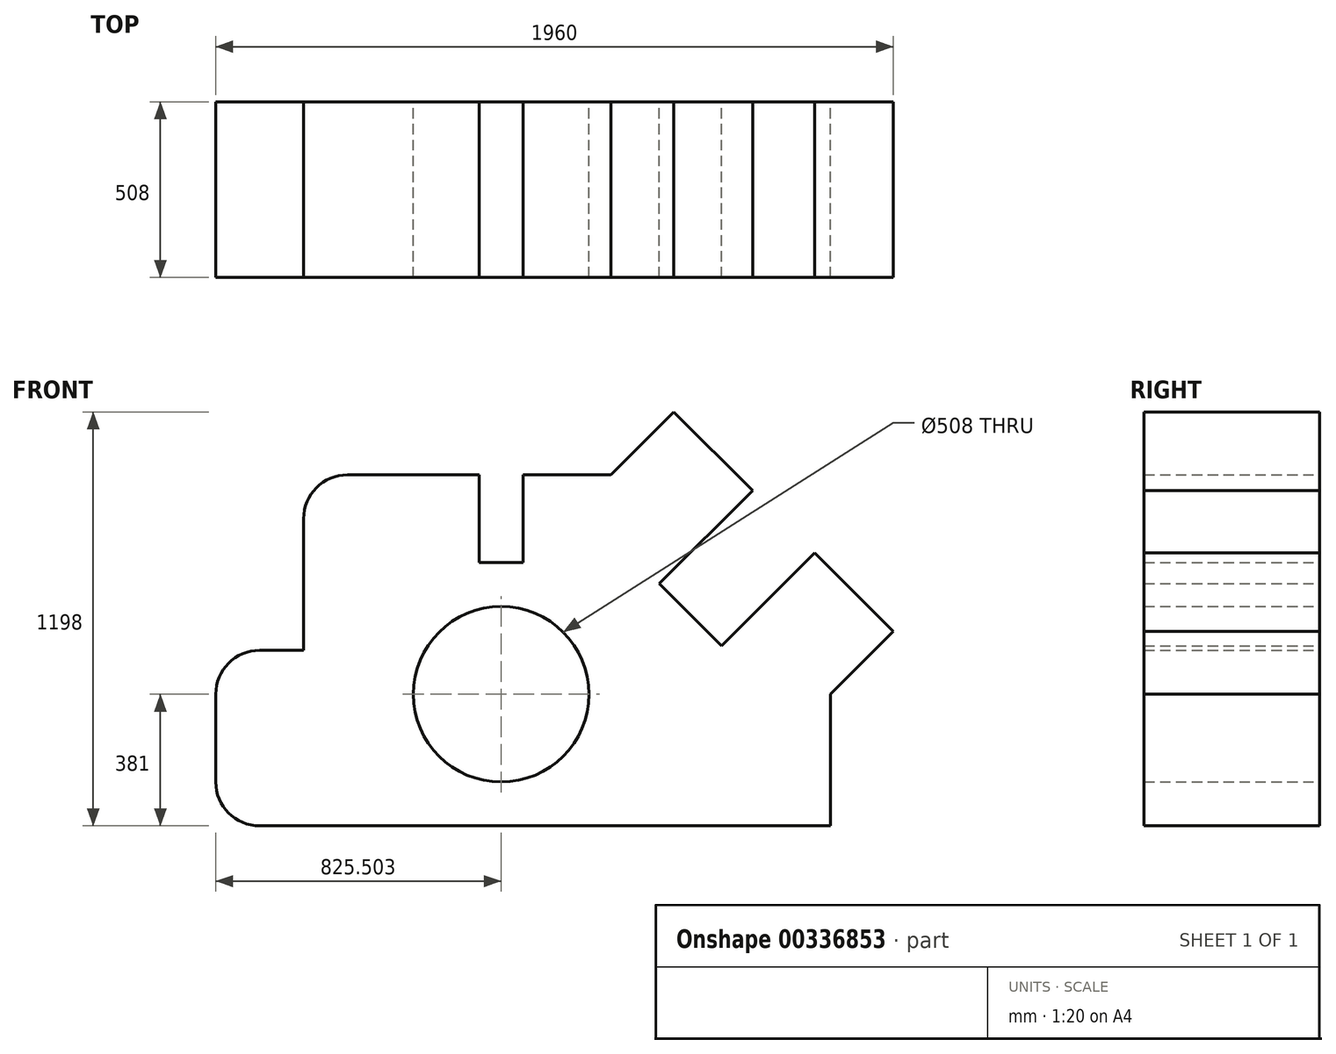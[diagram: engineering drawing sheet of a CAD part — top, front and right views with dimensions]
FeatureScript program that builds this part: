
annotation { "Feature Type Name" : "Feature", "Feature Type Description" : "" }
export const myFeature = defineFeature(function(context is Context, id is Id, definition is map)
    precondition{}
    {
        {
            var Q0;
            Q0=qCreatedBy(makeId("Front.planeOp"),FACE);
            var sketch = newSketch(context, id + "F0", { "sketchPlane" : qUnion([Q0])});
            skLineSegment(sketch, "E0", {"start": v(-303.19, 523.37) * mm, "end": v(-684.19, 523.37) * mm});
            skLineSegment(sketch, "E1", {"start": v(-811.19, 396.37) * mm, "end": v(-811.19, 15.37) * mm});
            skLineSegment(sketch, "E2", {"start": v(-811.19, 15.37) * mm, "end": v(-938.19, 15.37) * mm});
            skLineSegment(sketch, "E3", {"start": v(-1065.19, -111.63) * mm, "end": v(-1065.19, -365.63) * mm});
            skLineSegment(sketch, "E4", {"start": v(-938.19, -492.63) * mm, "end": v(712.81, -492.63) * mm});
            skLineSegment(sketch, "E5", {"start": v(712.81, -492.63) * mm, "end": v(712.81, -111.63) * mm});
            skLineSegment(sketch, "E6", {"start": v(712.81, -111.63) * mm, "end": v(894.81, 70.37) * mm});
            skLineSegment(sketch, "E7", {"start": v(894.81, 70.37) * mm, "end": v(667.12, 298.07) * mm});
            skLineSegment(sketch, "E8", {"start": v(667.12, 298.07) * mm, "end": v(397.7, 28.66) * mm});
            skLineSegment(sketch, "E9", {"start": v(397.7, 28.66) * mm, "end": v(218.1, 208.27) * mm});
            skLineSegment(sketch, "E10", {"start": v(218.1, 208.27) * mm, "end": v(487.51, 477.67) * mm});
            skLineSegment(sketch, "E11", {"start": v(487.51, 477.67) * mm, "end": v(259.81, 705.37) * mm});
            skLineSegment(sketch, "E12", {"start": v(259.81, 705.37) * mm, "end": v(77.81, 523.37) * mm});
            skLineSegment(sketch, "E13", {"start": v(77.81, 523.37) * mm, "end": v(-176.19, 523.37) * mm});
            skLineSegment(sketch, "E14", {"start": v(-176.19, 523.37) * mm, "end": v(-176.19, 269.37) * mm});
            skLineSegment(sketch, "E15", {"start": v(-176.19, 269.37) * mm, "end": v(-303.19, 269.37) * mm});
            skLineSegment(sketch, "E16", {"start": v(-303.19, 269.37) * mm, "end": v(-303.19, 523.37) * mm});
            skCircle(sketch, "E17", {"center": v(-239.69, -111.63) * mm, "radius": 254 * mm});
            skPoint(sketch, "E18.visualSharp", {"position": v(-811.19, 523.37) * mm});
            skArc(sketch, "E18.filletArc", {"start": v(-684.19, 523.37) * mm, "mid": v(-773.99, 486.17) * mm, "end": v(-811.19, 396.37) * mm});
            skPoint(sketch, "E19.visualSharp", {"position": v(-1065.19, 15.37) * mm});
            skArc(sketch, "E19.filletArc", {"start": v(-938.19, 15.37) * mm, "mid": v(-1027.99, -21.83) * mm, "end": v(-1065.19, -111.63) * mm});
            skPoint(sketch, "E20.visualSharp", {"position": v(-1065.19, -492.63) * mm});
            skArc(sketch, "E20.filletArc", {"start": v(-1065.19, -365.63) * mm, "mid": v(-1027.99, -455.43) * mm, "end": v(-938.19, -492.63) * mm});
            skSolve(sketch);
        }
        {
            var Q0;
            Q0=makeQuery(id+"F0.imprint","IMPRINT",FACE,{"disambiguationData":[TD([[makeQuery(id+"F0.imprint","IMPRINT",EDGE,{"derivedFrom":sQuery(id+"F0.wireOp",EDGE,"E0")}),1.0]])]});
            extrude(context, id + "F1", {"entities" : qUnion([Q0]), "depth" : 508 * mm});
        }
    });
